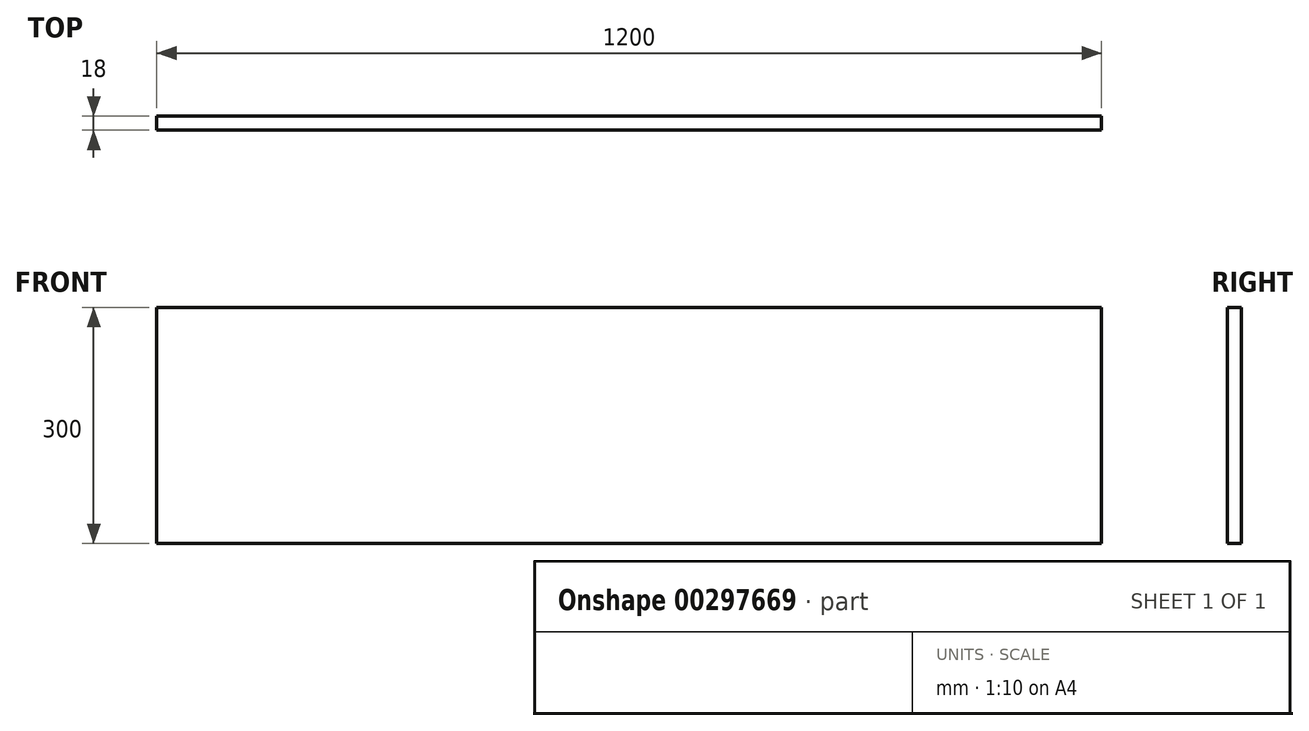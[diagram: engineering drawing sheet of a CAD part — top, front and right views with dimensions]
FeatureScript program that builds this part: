
annotation { "Feature Type Name" : "Feature", "Feature Type Description" : "" }
export const myFeature = defineFeature(function(context is Context, id is Id, definition is map)
    precondition{}
    {
        {
            var Q0;
            Q0=qCreatedBy(makeId("Front.planeOp"),FACE);
            var sketch = newSketch(context, id + "F0", { "sketchPlane" : qUnion([Q0])});
            skLineSegment(sketch, "E0.bottom", {"start": v(-606.1, 99.37) * mm, "end": v(593.9, 99.37) * mm});
            skLineSegment(sketch, "E0.top", {"start": v(-606.1, -200.63) * mm, "end": v(593.9, -200.63) * mm});
            skLineSegment(sketch, "E0.left", {"start": v(-606.1, 99.37) * mm, "end": v(-606.1, -200.63) * mm});
            skLineSegment(sketch, "E0.right", {"start": v(593.9, 99.37) * mm, "end": v(593.9, -200.63) * mm});
            skSolve(sketch);
        }
        {
            var Q0;
            Q0 = qSketchRegion(id + "F0", true);
            extrude(context, id + "F1", {"entities" : qUnion([Q0]), "depth" : 18 * mm, "offsetDistance" : 25 * mm});
        }
    });
